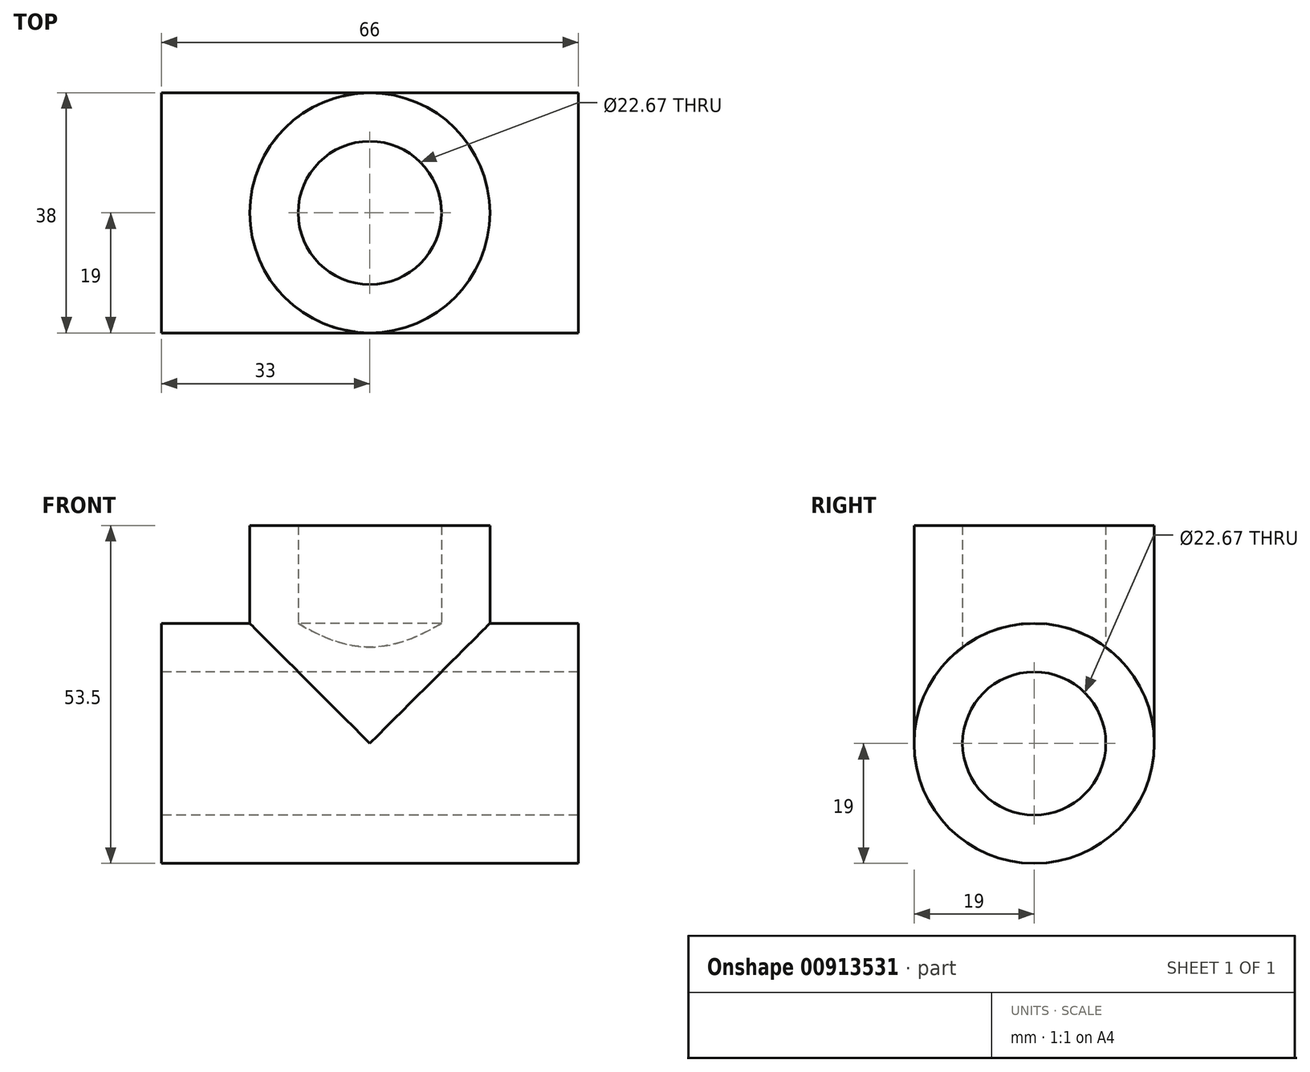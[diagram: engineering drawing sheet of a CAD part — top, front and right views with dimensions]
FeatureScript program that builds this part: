
annotation { "Feature Type Name" : "Feature", "Feature Type Description" : "" }
export const myFeature = defineFeature(function(context is Context, id is Id, definition is map)
    precondition{}
    {
        {
            var Q0;
            Q0=qCreatedBy(makeId("Right.planeOp"),FACE);
            var sketch = newSketch(context, id + "F0", { "sketchPlane" : qUnion([Q0])});
            skCircle(sketch, "E0", {"center": v(0, 0) * mm, "radius": 19 * mm});
            skCircle(sketch, "E1", {"center": v(0, 0) * mm, "radius": 11.34 * mm});
            skSolve(sketch);
        }
        {
            var Q0;
            Q0 = qSketchRegion(id + "F0", true);
            extrude(context, id + "F1", {"entities" : qUnion([Q0]), "depth" : 66 / 2 * mm, "offsetDistance" : 25 * mm, "hasSecondDirection" : true, "secondDirectionOppositeDirection" : true, "secondDirectionDepth" : (66 / 2) * mm});
        }
        {
            var Q0;
            Q0=qCreatedBy(makeId("Top.planeOp"),FACE);
            var sketch = newSketch(context, id + "F2", { "sketchPlane" : qUnion([Q0])});
            skCircle(sketch, "E2", {"center": v(0, 0) * mm, "radius": 11.34 * mm});
            skCircle(sketch, "E3", {"center": v(0, 0) * mm, "radius": 19 * mm});
            skSolve(sketch);
        }
        {
            var Q0;
            Q0 = qSketchRegion(id + "F2", true);
            extrude(context, id + "F3", {"entities" : qUnion([Q0]), "operationType" : NewBodyOperationType.ADD, "depth" : 34.5 * mm, "offsetDistance" : 25 * mm});
        }
        {
            var Q0;
            Q0=makeQuery(id+"F0.imprint","IMPRINT",FACE,{"disambiguationData":[TD([[makeQuery(id+"F0.imprint","IMPRINT",EDGE,{"derivedFrom":sQuery(id+"F0.wireOp",EDGE,"E1")}),1.0]])]});
            extrude(context, id + "F4", {"entities" : qUnion([Q0]), "operationType" : NewBodyOperationType.REMOVE, "oppositeDirection" : true, "depth" : 25 * mm, "offsetDistance" : 25 * mm, "hasSecondDirection" : true, "secondDirectionOppositeDirection" : false, "secondDirectionDepth" : 25 * mm});
        }
    });
